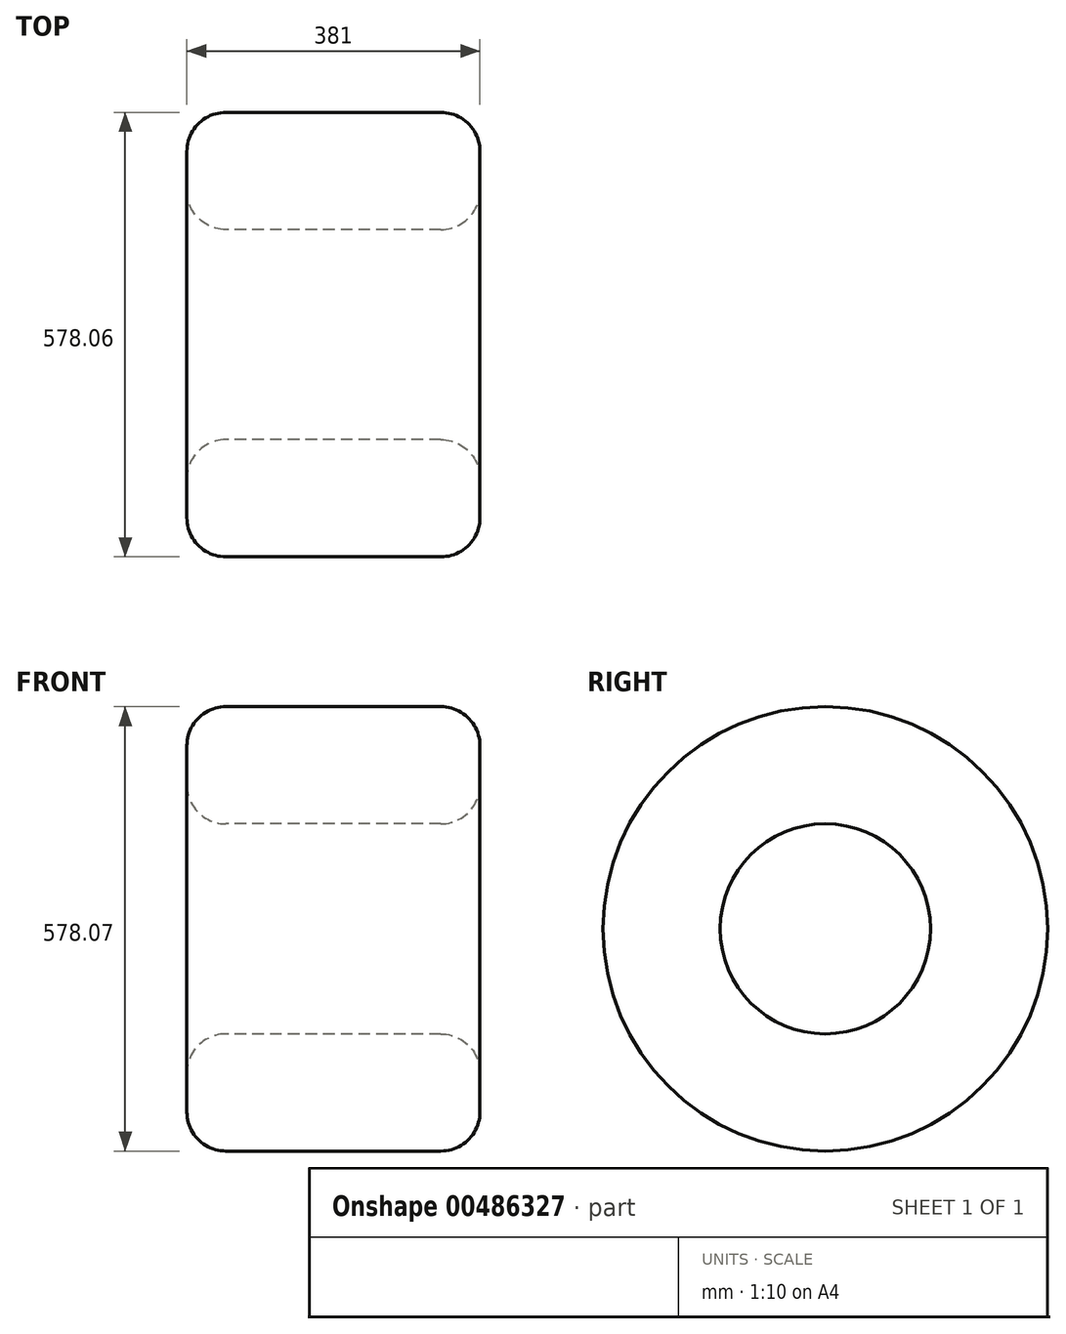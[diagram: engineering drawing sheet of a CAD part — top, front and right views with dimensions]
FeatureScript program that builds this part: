
annotation { "Feature Type Name" : "Feature", "Feature Type Description" : "" }
export const myFeature = defineFeature(function(context is Context, id is Id, definition is map)
    precondition{}
    {
        {
            var Q0;
            Q0=qCreatedBy(makeId("Front.planeOp"),FACE);
            var sketch = newSketch(context, id + "F0", { "sketchPlane" : qUnion([Q0])});
            skLineSegment(sketch, "E0.bottom", {"start": v(-153.93, -176.53) * mm, "end": v(125.47, -176.53) * mm});
            skLineSegment(sketch, "E0.top", {"start": v(-153.93, -328.93) * mm, "end": v(125.47, -328.93) * mm});
            skLineSegment(sketch, "E0.left", {"start": v(-204.73, -227.33) * mm, "end": v(-204.73, -278.13) * mm});
            skLineSegment(sketch, "E0.right", {"start": v(176.27, -227.33) * mm, "end": v(176.27, -278.13) * mm});
            skPoint(sketch, "E1.visualSharp", {"position": v(-204.73, -176.53) * mm});
            skArc(sketch, "E1.filletArc", {"start": v(-153.93, -176.53) * mm, "mid": v(-189.85, -191.4) * mm, "end": v(-204.73, -227.33) * mm});
            skPoint(sketch, "E2.visualSharp", {"position": v(-204.73, -328.93) * mm});
            skArc(sketch, "E2.filletArc", {"start": v(-204.73, -278.13) * mm, "mid": v(-189.85, -314.05) * mm, "end": v(-153.93, -328.93) * mm});
            skPoint(sketch, "E3.visualSharp", {"position": v(176.27, -176.53) * mm});
            skArc(sketch, "E3.filletArc", {"start": v(176.27, -227.33) * mm, "mid": v(161.39, -191.4) * mm, "end": v(125.47, -176.53) * mm});
            skPoint(sketch, "E4.visualSharp", {"position": v(176.27, -328.93) * mm});
            skArc(sketch, "E4.filletArc", {"start": v(125.47, -328.93) * mm, "mid": v(161.39, -314.05) * mm, "end": v(176.27, -278.13) * mm});
            skSolve(sketch);
        }
        {
            var Q0;
            Q0=qCreatedBy(makeId("Front.planeOp"),FACE);
            var sketch = newSketch(context, id + "F1", { "sketchPlane" : qUnion([Q0])});
            skPoint(sketch, "E5", {"position": v(-205.2, -379.73) * mm});
            skPoint(sketch, "E6", {"position": v(-154.18, -379.04) * mm});
            skLineSegment(sketch, "E7", {"start": v(-154.18, -379.04) * mm, "end": v(-199.43, -300.67) * mm});
            skLineSegment(sketch, "E8", {"start": v(125.22, -379.73) * mm, "end": v(170.66, -301.47) * mm});
            skLineSegment(sketch, "E9", {"start": v(-154.18, -379.04) * mm, "end": v(125.22, -379.73) * mm});
            skLineSegment(sketch, "E10", {"start": v(-201.61, -465.56) * mm, "end": v(208, -465.56) * mm});
            skSolve(sketch);
        }
        {
            var Q0;
            Q0=sQuery(id+"F1.wireOp",EDGE,"E7");
            var Q1;
            Q1=sQuery(id+"F1.wireOp",EDGE,"E9");
            var Q2;
            Q2=sQuery(id+"F1.wireOp",EDGE,"E8");
            var Q3;
            Q3=sQuery(id+"F1.wireOp",EDGE,"E10");
            revolve(context, id + "F2", {"bodyType" : ToolBodyType.SURFACE, "surfaceEntities" : qUnion([Q0, Q1, Q2]), "axis" : qUnion([Q3]), "revolveType" : RevolveType.FULL});
        }
        {
            var Q0;
            Q0=makeQuery(id+"F0.imprint","IMPRINT",FACE,{"disambiguationData":[TD([[makeQuery(id+"F0.imprint","IMPRINT",EDGE,{"derivedFrom":sQuery(id+"F0.wireOp",EDGE,"E0.bottom")}),-1.0]])]});
            var Q1;
            Q1=sQuery(id+"F1.wireOp",EDGE,"E10");
            revolve(context, id + "F3", {"entities" : qUnion([Q0]), "axis" : qUnion([Q1]), "revolveType" : RevolveType.FULL});
        }
    });
